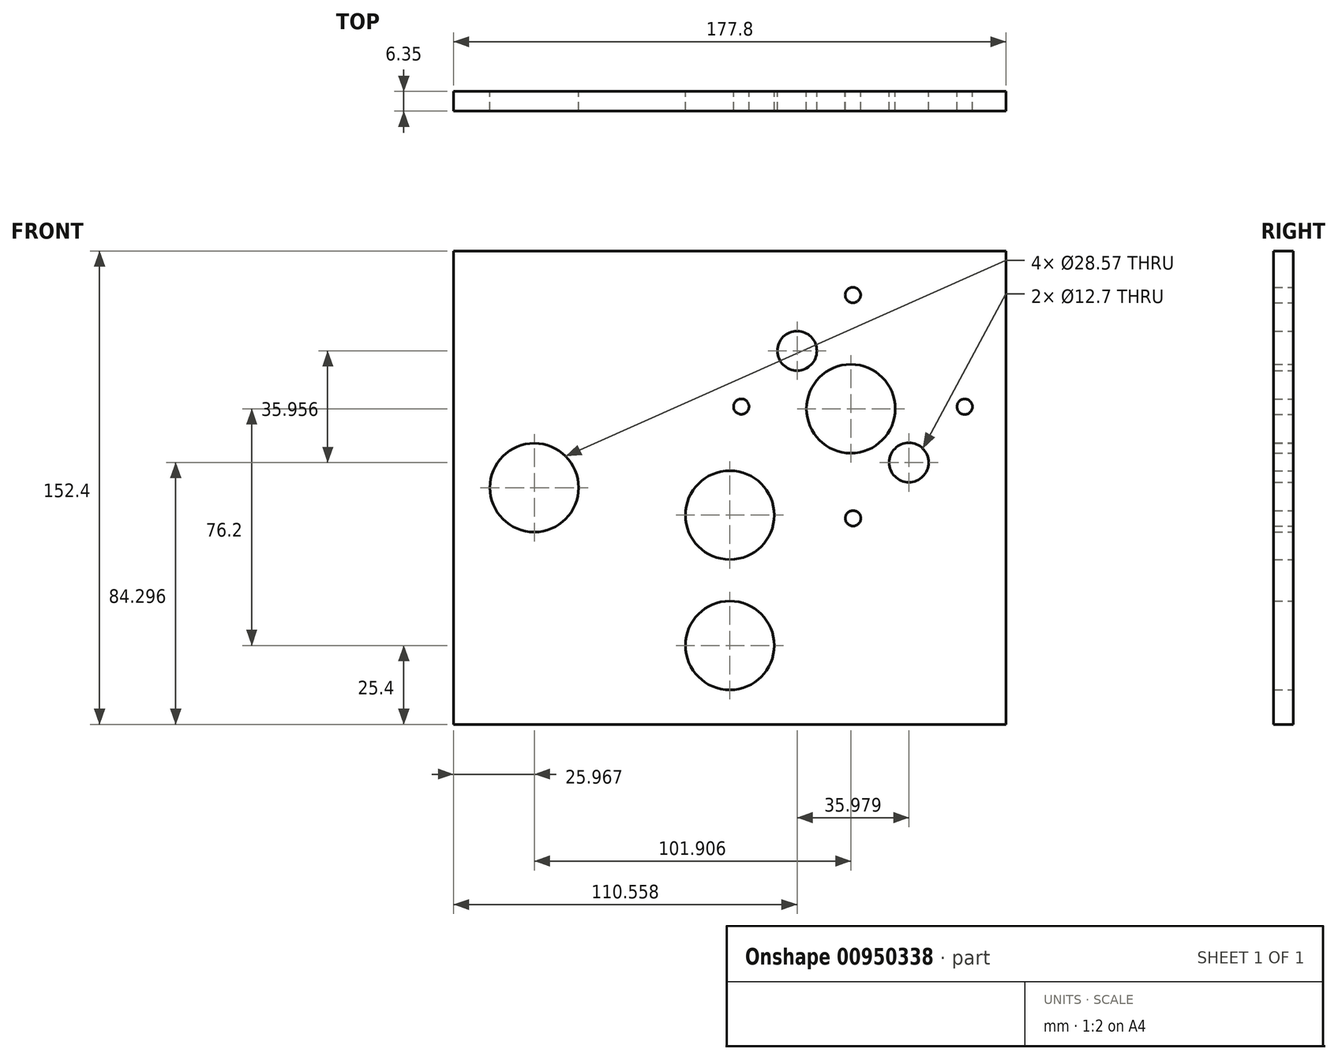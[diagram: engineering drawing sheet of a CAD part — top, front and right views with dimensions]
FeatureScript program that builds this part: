
annotation { "Feature Type Name" : "Feature", "Feature Type Description" : "" }
export const myFeature = defineFeature(function(context is Context, id is Id, definition is map)
    precondition{}
    {
        {
            var Q0;
            Q0=qCreatedBy(makeId("Front.planeOp"),FACE);
            var sketch = newSketch(context, id + "F0", { "sketchPlane" : qUnion([Q0])});
            skCircle(sketch, "E0", {"center": v(0, 0) * mm, "radius": 14.29 * mm});
            skLineSegment(sketch, "E1.bottom", {"start": v(88.9, -25.4) * mm, "end": v(-88.9, -25.4) * mm});
            skLineSegment(sketch, "E1.top", {"start": v(88.9, 127) * mm, "end": v(-88.9, 127) * mm});
            skLineSegment(sketch, "E1.left", {"start": v(88.9, -25.4) * mm, "end": v(88.9, 127) * mm});
            skLineSegment(sketch, "E1.right", {"start": v(-88.9, -25.4) * mm, "end": v(-88.9, 127) * mm});
            skCircle(sketch, "E2", {"center": v(0, 41.96) * mm, "radius": 14.29 * mm});
            skLineSegment(sketch, "E3", {"start": v(-88.9, 25.4) * mm, "end": v(88.9, 25.4) * mm});
            skCircle(sketch, "E4", {"center": v(-62.93, 50.8) * mm, "radius": 14.29 * mm});
            skCircle(sketch, "E5", {"center": v(38.97, 76.2) * mm, "radius": 14.29 * mm});
            skCircle(sketch, "E6", {"center": v(21.66, 94.85) * mm, "radius": 6.35 * mm});
            skCircle(sketch, "E7", {"center": v(3.7, 76.9) * mm, "radius": 2.49 * mm});
            skCircle(sketch, "E8", {"center": v(39.62, 112.81) * mm, "radius": 2.49 * mm});
            skLineSegment(sketch, "E9", {"start": v(21.66, 94.85) * mm, "end": v(39.62, 112.81) * mm});
            skLineSegment(sketch, "E10", {"start": v(3.7, 76.9) * mm, "end": v(21.66, 94.85) * mm});
            skCircle(sketch, "E11", {"center": v(57.64, 58.9) * mm, "radius": 6.35 * mm});
            skCircle(sketch, "E12", {"center": v(39.68, 40.94) * mm, "radius": 2.49 * mm});
            skCircle(sketch, "E13", {"center": v(75.6, 76.86) * mm, "radius": 2.49 * mm});
            skLineSegment(sketch, "E14", {"start": v(39.68, 40.94) * mm, "end": v(57.64, 58.9) * mm});
            skLineSegment(sketch, "E15", {"start": v(75.6, 76.86) * mm, "end": v(57.64, 58.9) * mm});
            skSolve(sketch);
        }
        {
            var Q0;
            {var subQ1=sQuery(id+"F0.wireOp",EDGE,"E1.top");Q0=makeQuery(id+"F0.imprint","IMPRINT",FACE,{"disambiguationData":[TD([[makeQuery(id+"F0.imprint","IMPRINT",EDGE,{"derivedFrom":subQ1}),1.0]])]});}
            var Q1;
            Q1=makeQuery(id+"F0.imprint","IMPRINT",FACE,{"disambiguationData":[TD([[makeQuery(id+"F0.imprint","IMPRINT",EDGE,{"derivedFrom":sQuery(id+"F0.wireOp",EDGE,"E0")}),-1.0]])]});
            extrude(context, id + "F1", {"entities" : qUnion([Q0, Q1]), "depth" : 6.35 * mm, "offsetDistance" : 25.4 * mm});
        }
    });
